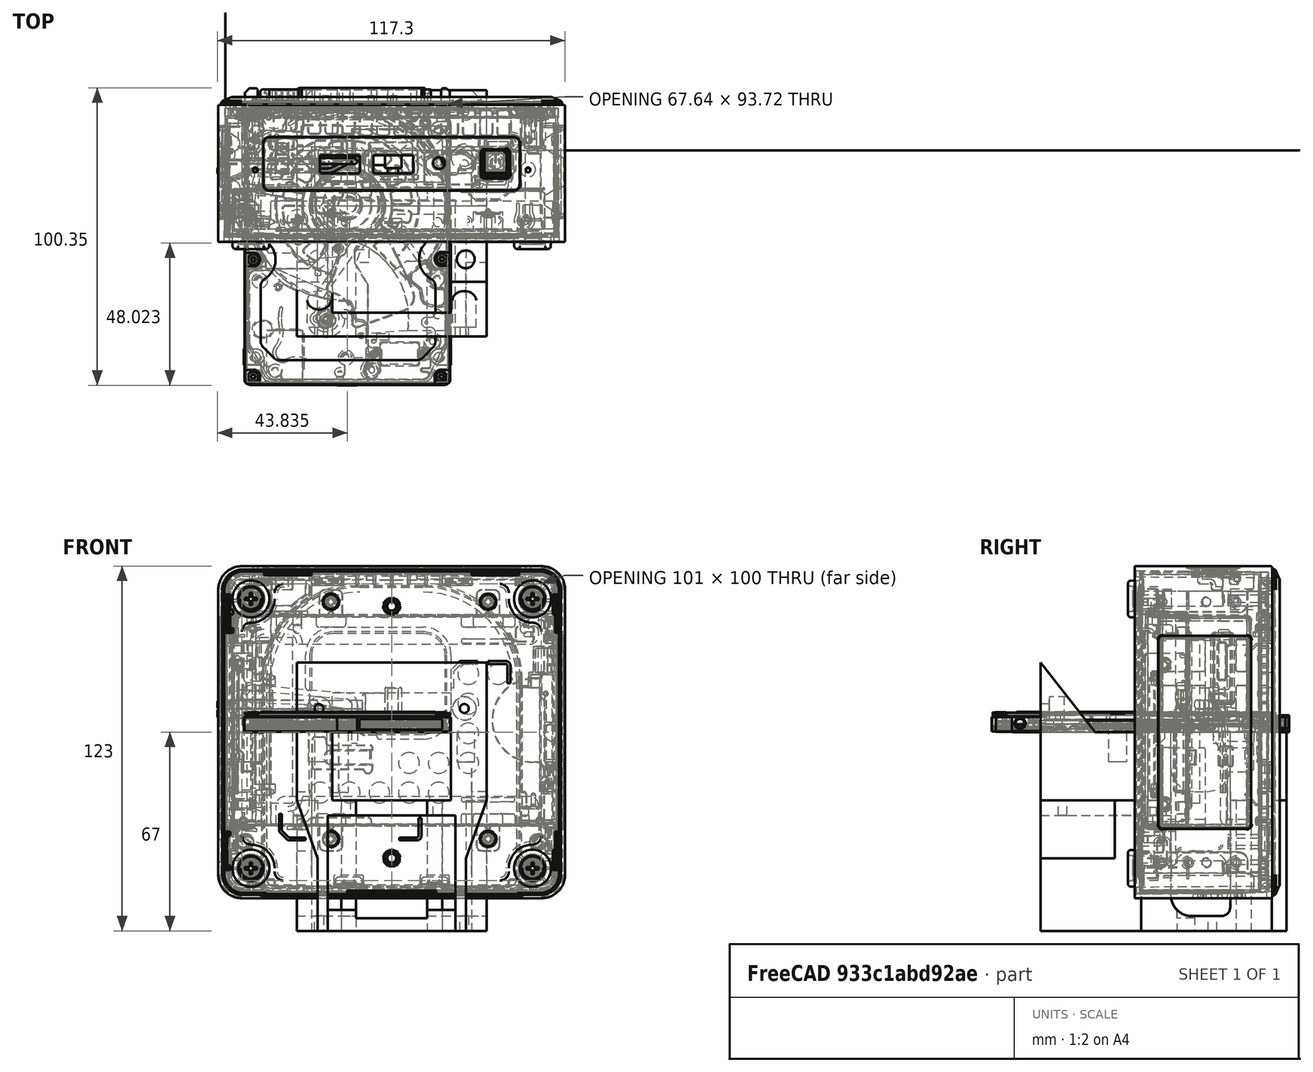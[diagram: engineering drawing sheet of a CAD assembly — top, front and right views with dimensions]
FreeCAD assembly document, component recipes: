
FREECAD ASSEMBLY — COMPONENT RECIPES ("RobotBody")

This assembly document has 14 components, labeled P0..P13 below (a component is one placed body or linked part). 12 of them carry a construction recipe — the FreeCAD feature program that regenerates the part from scratch, quoted from this document or its linked companion documents; the rest are supplied as boundary geometry only. No exploded tour is included for this assembly.
COMPONENT P0 — recipe-attached ("BodyHolder001", modeled in this document).
Construction recipe (the document's own serialized feature program — sketch geometry with constraints, then the solid features built on it; lengths are millimeters unless a unit is written):

FEATURE [Sketcher::SketchObject] Sketch022
  ArcFitTolerance = 1e-06
  AttachmentSupport = -> [XY_Plane002]
  FullyConstrained = false
  MakeInternals = false
  MapMode = 5
  expr: Constraints[10] = <<SpreadSheet001>>.BaseWidth
  expr: Constraints[18] = <<SpreadSheet001>>.BaseRectWidth
  expr: Constraints[23] = <<SpreadSheet001>>.BaseWidth / 2
  sketch-geometry (10):
    g0: GeomPoint [constr] X=0 Y=0 Z=0
    g1: LineSegment StartX=32 StartY=-51 StartZ=0 EndX=32 EndY=32 EndZ=0
    g2: LineSegment StartX=32 StartY=32 StartZ=0 EndX=-32 EndY=32 EndZ=0
    g3: LineSegment StartX=-32 StartY=32 StartZ=0 EndX=-32 EndY=-51 EndZ=0
    g4: LineSegment StartX=-32 StartY=-51 StartZ=0 EndX=-20 EndY=-51 EndZ=0
    g5: GeomPoint [constr] X=0 Y=0 Z=0
    g6: LineSegment StartX=20 StartY=-51 StartZ=0 EndX=32 EndY=-51 EndZ=0
    g7: LineSegment StartX=-20 StartY=20 StartZ=0 EndX=-20 EndY=-51 EndZ=0
    g8: LineSegment StartX=20 StartY=20 StartZ=0 EndX=20 EndY=-51 EndZ=0
    g9: LineSegment StartX=-20 StartY=20 StartZ=0 EndX=20 EndY=20 EndZ=0
  constraints (25):
    c: Coincident(g0,g-1)
    c: Coincident(g1,g2)
    c: Coincident(g2,g3)
    c: Coincident(g3,g4)
    c: Coincident(g6,g1)
    c: Vertical(g1)
    c: Vertical(g3)
    c: Horizontal(g2)
    c: Horizontal(g4)
    c: Coincident(g5,g0)
    c: DistanceX(g2,g2) = 64
    c: Horizontal(g6,g1)
    c: Coincident(g7,g4)
    c: Vertical(g7)
    c: Coincident(g8,g6)
    c: Vertical(g8)
    c: Horizontal(g8,g7)
    c: Horizontal(g4,g6)
    c: Distance(g8,g7) = 40
    c: Equal(g4,g6)
    c: Coincident(g7,g9)
    c: Coincident(g9,g8)
    c: Distance(g2,g9) = 12
    c: Distance(g-1,g2) = 32
    c: Distance(g-1,g4) = 51
FEATURE [PartDesign::Pad] Pad009
  Direction = (0,0,1)
  Length = 23
  Length2 = 10
  Profile = -> Sketch022
  ReferenceAxis = -> Sketch022 [N_Axis]
  Refine = true
  Reversed = true
  Suppressed = false
  Type = 0
  expr: Length = <<SpreadSheet001>>.MainShaftHolder
FEATURE [Sketcher::SketchObject] Sketch023
  ArcFitTolerance = 1e-06
  AttachmentSupport = -> [Pad009]
  FullyConstrained = false
  MakeInternals = false
  MapMode = 5
  Placement = pos=(0,0,-23) rot=(1,0,0;3.14159rad)
  sketch-geometry (9):
    g0: LineSegment StartX=-25 StartY=51 StartZ=0 EndX=-25 EndY=-1 EndZ=0
    g1: LineSegment StartX=-25 StartY=-1 StartZ=0 EndX=25 EndY=-1 EndZ=0
    g2: LineSegment StartX=25 StartY=-1 StartZ=0 EndX=25 EndY=51 EndZ=0
    g3: LineSegment StartX=25 StartY=51 StartZ=0 EndX=12 EndY=51 EndZ=0
    g4: GeomPoint [constr] X=0 Y=28 Z=0
    g5: ArcOfCircle CenterX=0 CenterY=28 CenterZ=0 NormalX=0 NormalY=0 NormalZ=1 AngleXU=0 Radius=12 StartAngle=3.14094 EndAngle=6.28253
    g6: LineSegment StartX=-12 StartY=28.0078 StartZ=0 EndX=-12 EndY=51 EndZ=0
    g7: LineSegment StartX=12 StartY=27.9922 StartZ=0 EndX=12 EndY=51 EndZ=0
    g8: LineSegment StartX=-12 StartY=51 StartZ=0 EndX=-25 EndY=51 EndZ=0
  constraints (24):
    c: Coincident(g0,g1)
    c: Coincident(g1,g2)
    c: Coincident(g2,g3)
    c: Coincident(g8,g0)
    c: Vertical(g0)
    c: Vertical(g2)
    c: Horizontal(g1)
    c: PointOnObject(g4,g-2)
    c: DistanceY(g-1,g4) = 28
    c: DistanceX(g8,g3) = 50
    c: Angle(g5) = 3.14159
    c: Coincident(g5,g4)
    c: Vertical(g6)
    c: Coincident(g6,g5)
    c: Radius(g5) = 12
    c: Coincident(g5,g7)
    c: Coincident(g7,g3)
    c: Vertical(g7)
    c: Equal(g0,g2)
    c: Horizontal(g3)
    c: Horizontal(g8)
    c: Coincident(g6,g8)
    c: Distance(g4,g3) = 23
    c: Distance(g4,g1) = 29
FEATURE [PartDesign::Pad] Pad010
  BaseFeature = -> Pad009
  Direction = (0,0,-1)
  Length = 44
  Length2 = 10
  Profile = -> Sketch023
  ReferenceAxis = -> Sketch023 [N_Axis]
  Refine = true
  Suppressed = false
  Type = 0
FEATURE [Sketcher::SketchObject] Sketch024
  ArcFitTolerance = 1e-06
  AttachmentSupport = -> [Pad010]
  FullyConstrained = false
  MakeInternals = false
  MapMode = 5
  Placement = pos=(0,-51,0) rot=(1,0,0;1.5708rad)
  sketch-geometry (5):
    g0: LineSegment StartX=21.4848 StartY=-78 StartZ=0 EndX=21.4848 EndY=-28 EndZ=0
    g1: LineSegment StartX=21.4848 StartY=-28 StartZ=0 EndX=-21.5152 EndY=-28 EndZ=0
    g2: LineSegment StartX=-21.5152 StartY=-28 StartZ=0 EndX=-21.5152 EndY=-78 EndZ=0
    g3: LineSegment StartX=-21.5152 StartY=-78 StartZ=0 EndX=21.4848 EndY=-78 EndZ=0
    g4: GeomPoint [constr] X=-0.0151564 Y=-53 Z=0
  constraints (12):
    c: Coincident(g0,g1)
    c: Coincident(g1,g2)
    c: Coincident(g2,g3)
    c: Coincident(g3,g0)
    c: Vertical(g0)
    c: Vertical(g2)
    c: Horizontal(g1)
    c: Horizontal(g3)
    c: Symmetric(g2,g0,g4)
    c: DistanceY(g2,g2) = 50
    c: DistanceX(g1,g1) = 43
    c: Distance(g-1,g1) = 28
FEATURE [PartDesign::Pocket] Pocket012
  BaseFeature = -> Pad010
  Direction = (0,1,-2e-16)
  Length = 46
  Length2 = 5
  Profile = -> Sketch024
  ReferenceAxis = -> Sketch024 [N_Axis]
  Refine = true
  Suppressed = false
  Type = 0
FEATURE [Sketcher::SketchObject] Sketch025
  ArcFitTolerance = 1e-06
  AttachmentSupport = -> [Pocket012]
  ExternalGeometry = -> [Pocket012]
  FullyConstrained = false
  MakeInternals = false
  MapMode = 5
  Placement = pos=(0,-51,0) rot=(1,0,0;1.5708rad)
  sketch-geometry (6):
    g0: LineSegment StartX=-32 StartY=-23 StartZ=0 EndX=-25 EndY=-23 EndZ=0
    g1: LineSegment StartX=-25 StartY=-23 StartZ=0 EndX=-25 EndY=-42.5619 EndZ=0
    g2: LineSegment StartX=-25 StartY=-42.5619 StartZ=0 EndX=-32 EndY=-23 EndZ=0
    g3: LineSegment StartX=32 StartY=-23 StartZ=0 EndX=25 EndY=-23 EndZ=0
    g4: LineSegment StartX=25 StartY=-42.5619 StartZ=0 EndX=32 EndY=-23 EndZ=0
    g5: LineSegment StartX=25 StartY=-23 StartZ=0 EndX=25 EndY=-42.5619 EndZ=0
  constraints (13):
    c: Coincident(g-3,g0)
    c: Coincident(g0,g-4)
    c: Coincident(g0,g1)
    c: Vertical(g1)
    c: Coincident(g1,g2)
    c: Coincident(g2,g0)
    c: Coincident(g-6,g3)
    c: Coincident(g3,g-6)
    c: Coincident(g4,g3)
    c: Coincident(g3,g5)
    c: Coincident(g5,g4)
    c: Vertical(g5)
    c: Horizontal(g1,g4)
FEATURE [PartDesign::Pad] Pad011
  BaseFeature = -> Pocket012
  Direction = (0,-1,2e-16)
  Length = 25
  Length2 = 10
  Profile = -> Sketch025
  ReferenceAxis = -> Sketch025 [N_Axis]
  Refine = true
  Reversed = true
  Suppressed = false
  Type = 0
FEATURE [Sketcher::SketchObject] Sketch026
  ArcFitTolerance = 1e-06
  AttachmentSupport = -> [Pad011]
  FullyConstrained = true
  MakeInternals = false
  MapMode = 5
  Placement = pos=(0,0,-23) rot=(0,0,1;0rad)
  expr: Constraints[10] = <<SpreadSheet001>>.StepperCenterToScewHole
  expr: Constraints[11] = <<SpreadSheet001>>.StepperCenterToScewHole
  expr: Constraints[12] = <<SpreadSheet001>>.StepperCenterToScewHole
  expr: Constraints[13] = <<SpreadSheet001>>.StepperCenterToScewHole
  expr: Constraints[3] = <<SpreadSheet001>>.StepperCenterToScewHole
  expr: Constraints[4] = <<SpreadSheet001>>.StepperCenterToScewHole
  expr: Constraints[8] = <<SpreadSheet001>>.StepperCenterToScewHole
  expr: Constraints[9] = <<SpreadSheet001>>.StepperCenterToScewHole
  sketch-geometry (5):
    g0: GeomPoint [constr] X=0 Y=-28 Z=0
    g1: Circle CenterX=-15.5 CenterY=-12.5 CenterZ=0 NormalX=0 NormalY=0 NormalZ=1 AngleXU=0 Radius=1.5
    g2: Circle CenterX=-15.5 CenterY=-43.5 CenterZ=0 NormalX=0 NormalY=0 NormalZ=1 AngleXU=0 Radius=1.5
    g3: Circle CenterX=15.5 CenterY=-43.5 CenterZ=0 NormalX=0 NormalY=0 NormalZ=1 AngleXU=0 Radius=1.5
    g4: Circle CenterX=15.5 CenterY=-12.5 CenterZ=0 NormalX=0 NormalY=0 NormalZ=1 AngleXU=0 Radius=1.5
  constraints (14):
    c: PointOnObject(g0,g-2)
    c: DistanceY(g0,g-1) = 28
    c: Diameter(g1) = 3
    c: Distance(g1,g-2) = 15.5
    c: DistanceY(g0,g1) = 15.5
    c: Diameter(g2) = 3
    c: Diameter(g3) = 3
    c: Diameter(g4) = 3
    c: Distance(g4,g-2) = 15.5
    c: DistanceY(g0,g4) = 15.5
    c: DistanceY(g3,g0) = 15.5
    c: DistanceY(g2,g0) = 15.5
    c: DistanceX(g2,g0) = 15.5
    c: DistanceX(g0,g3) = 15.5
FEATURE [PartDesign::Pocket] Pocket013
  BaseFeature = -> Pad011
  Direction = (0,0,-1)
  Length = 10
  Length2 = 5
  Profile = -> Sketch026
  ReferenceAxis = -> Sketch026 [N_Axis]
  Refine = true
  Suppressed = false
  Type = 1
FEATURE [Sketcher::SketchObject] Sketch027
  ArcFitTolerance = 1e-06
  AttachmentSupport = -> [Pocket013]
  FullyConstrained = true
  MakeInternals = false
  MapMode = 5
  expr: Constraints[0] = 6
  expr: Constraints[1] = 25
  expr: Constraints[2] = 25 mm
  sketch-geometry (1):
    g0: Circle CenterX=-25 CenterY=25 CenterZ=0 NormalX=0 NormalY=0 NormalZ=1 AngleXU=0 Radius=3
  constraints (3):
    c: Diameter(g0) = 6
    c: Distance(g0,g-2) = 25
    c: Distance(g0,g-1) = 25
FEATURE [PartDesign::Pocket] Pocket014
  BaseFeature = -> Pocket013
  Direction = (0,0,-1)
  Length = 10
  Length2 = 5
  Profile = -> Sketch027
  ReferenceAxis = -> Sketch027 [N_Axis]
  Refine = true
  Suppressed = false
  Type = 0
FEATURE [PartDesign::PolarPattern] PolarPattern001
  Angle = 360
  Axis = -> Sketch027 [N_Axis]
  BaseFeature = -> Pocket014
  Mode = 0
  Occurrences = 4
  Offset = 120
  Originals = -> [Pocket014]
  Refine = true
  Suppressed = false
  TransformMode = 0
FEATURE [Sketcher::SketchObject] Sketch028
  ArcFitTolerance = 1e-06
  AttachmentSupport = -> [PolarPattern001]
  FullyConstrained = false
  MakeInternals = false
  MapMode = 5
  Placement = pos=(0,1,0) rot=(0,0.707107,0.707107;3.14159rad)
  sketch-geometry (4):
    g0: LineSegment StartX=-12 StartY=-62.7172 StartZ=0 EndX=12 EndY=-62.7172 EndZ=0
    g1: LineSegment StartX=12 StartY=-62.7172 StartZ=0 EndX=12 EndY=-49.3568 EndZ=0
    g2: LineSegment StartX=-12 StartY=-49.3568 StartZ=0 EndX=-12 EndY=-62.7172 EndZ=0
    g3: ArcOfCircle CenterX=5.51344e-07 CenterY=-49.3568 CenterZ=0 NormalX=0 NormalY=0 NormalZ=1 AngleXU=0 Radius=12 StartAngle=4e-16 EndAngle=3.14159
  constraints (10):
    c: Coincident(g0,g1)
    c: Coincident(g2,g0)
    c: Horizontal(g0)
    c: Vertical(g1)
    c: Vertical(g2)
    c: Distance(g1,g2) = 24
    c: Coincident(g0,g-3)
    c: Symmetric(g1,g2,g3)
    c: Coincident(g3,g2)
    c: Coincident(g3,g1)
FEATURE [PartDesign::Pocket] Pocket011
  BaseFeature = -> PolarPattern001
  Direction = (0,-1,2e-16)
  Length = 6
  Length2 = 5
  Profile = -> Sketch028
  ReferenceAxis = -> Sketch028 [N_Axis]
  Refine = true
  Suppressed = false
  Type = 0
FEATURE [Sketcher::SketchObject] Sketch021
  ArcFitTolerance = 1e-06
  AttachmentSupport = -> [Pocket011]
  FullyConstrained = true
  MakeInternals = false
  MapMode = 5
  Placement = pos=(0,0,-23) rot=(1,0,0;3.14159rad)
  sketch-geometry (16):
    g0: LineSegment StartX=-32 StartY=17 StartZ=0 EndX=-25 EndY=17 EndZ=0
    g1: LineSegment StartX=-25 StartY=17 StartZ=0 EndX=-25 EndY=7 EndZ=0
    g2: LineSegment StartX=-25 StartY=7 StartZ=0 EndX=-17 EndY=-1 EndZ=0
    g3: LineSegment StartX=-17 StartY=-1 StartZ=0 EndX=-17 EndY=-15 EndZ=0
    g4: LineSegment StartX=-17 StartY=-15 StartZ=0 EndX=-12 EndY=-20 EndZ=0
    g5: LineSegment StartX=-12 StartY=-20 StartZ=0 EndX=12 EndY=-20 EndZ=0
    g6: LineSegment StartX=12 StartY=-20 StartZ=0 EndX=17 EndY=-15 EndZ=0
    g7: LineSegment StartX=17 StartY=-15 StartZ=0 EndX=17 EndY=-1 EndZ=0
    g8: LineSegment StartX=17 StartY=-1 StartZ=0 EndX=25 EndY=7 EndZ=0
    g9: LineSegment StartX=25 StartY=7 StartZ=0 EndX=25 EndY=17 EndZ=0
    g10: LineSegment StartX=25 StartY=17 StartZ=0 EndX=32 EndY=17 EndZ=0
    g11: LineSegment StartX=32 StartY=17 StartZ=0 EndX=32 EndY=-27 EndZ=0
    g12: LineSegment StartX=32 StartY=-27 StartZ=0 EndX=27 EndY=-32 EndZ=0
    g13: LineSegment StartX=27 StartY=-32 StartZ=0 EndX=-27 EndY=-32 EndZ=0
    g14: LineSegment StartX=-27 StartY=-32 StartZ=0 EndX=-32 EndY=-27 EndZ=0
    g15: LineSegment StartX=-32 StartY=-27 StartZ=0 EndX=-32 EndY=17 EndZ=0
  constraints (48):
    c: Horizontal(g0)
    c: Coincident(g0,g1)
    c: Vertical(g1)
    c: Coincident(g1,g2)
    c: Coincident(g2,g3)
    c: Vertical(g3)
    c: Coincident(g3,g4)
    c: Coincident(g4,g5)
    c: Horizontal(g5)
    c: Coincident(g5,g6)
    c: Coincident(g6,g7)
    c: Vertical(g7)
    c: Coincident(g7,g8)
    c: Coincident(g8,g9)
    c: Vertical(g9)
    c: Coincident(g9,g10)
    c: Horizontal(g10)
    c: Coincident(g10,g11)
    c: Vertical(g11)
    c: Coincident(g11,g12)
    c: Coincident(g12,g13)
    c: Horizontal(g13)
    c: Coincident(g13,g14)
    c: Coincident(g14,g15)
    c: Coincident(g15,g0)
    c: Vertical(g15)
    c: Distance(g-2,g15) = 32
    c: Distance(g-1,g0) = 17
    c: Distance(g0,g0) = 7
    c: DistanceY(g1,g1) = 10
    c: Distance(g15,g3) = 15
    c: Angle(g2,g1) = 2.35619
    c: Angle(g14,g15) = 2.35619
    c: Distance(g-1,g13) = 32
    c: DistanceX(g10,g10) = 7
    c: Distance(g-2,g11) = 32
    c: DistanceY(g9,g9) = 10
    c: Angle(g9,g8) = 2.35619
    c: Distance(g-1,g10) = 17
    c: Distance(g7,g11) = 15
    c: DistanceY(g14,g-1) = 27
    c: DistanceY(g11,g-1) = 27
    c: Angle(g11,g12) = 2.35619
    c: Angle(g4,g3) = 2.35619
    c: Angle(g7,g6) = 2.35619
    c: Distance(g-1,g5) = 20
    c: DistanceX(g4,g-1) = 12
    c: Distance(g5,g-2) = 12
FEATURE [PartDesign::Pad] Pad008
  BaseFeature = -> Pocket011
  Direction = (0,0,-1)
  Length = 44
  Length2 = 10
  Profile = -> Sketch021
  ReferenceAxis = -> Sketch021 [N_Axis]
  Refine = true
  Suppressed = false
  Type = 0
FEATURE [Sketcher::SketchObject] Sketch029
  ArcFitTolerance = 1e-06
  AttachmentSupport = -> [Pad008]
  ExternalGeometry = -> [Pad008]
  FullyConstrained = true
  MakeInternals = false
  MapMode = 5
  Placement = pos=(-32,3.571e-13,-2.7539e-12) rot=(-0.57735,0.57735,0.57735;4.18879rad)
  sketch-geometry (5):
    g0: LineSegment StartX=7 StartY=0 StartZ=0 EndX=-13 EndY=0 EndZ=0
    g1: LineSegment StartX=7 StartY=-55 StartZ=0 EndX=7 EndY=0 EndZ=0
    g2: LineSegment StartX=-13 StartY=-62 StartZ=0 EndX=-13 EndY=0 EndZ=0
    g3: LineSegment StartX=-13 StartY=-62 StartZ=0 EndX=-1.8e-15 EndY=-62 EndZ=0
    g4: ArcOfCircle CenterX=0 CenterY=-55 CenterZ=0 NormalX=0 NormalY=0 NormalZ=1 AngleXU=0 Radius=7 StartAngle=4.71239 EndAngle=6.28319
  constraints (16):
    c: Horizontal(g0)
    c: Coincident(g1,g0)
    c: Vertical(g1)
    c: Distance(g0,g-2) = 13
    c: DistanceY(g1,g1) = 55
    c: Coincident(g2,g0)
    c: Vertical(g2)
    c: Coincident(g2,g3)
    c: DistanceX(g3,g3) = 13
    c: Horizontal(g3)
    c: Distance(g-3,g3) = 5
    c: Horizontal(g0,g-1)
    c: PointOnObject(g4,g-2)
    c: Coincident(g4,g1)
    c: Coincident(g3,g4)
    c: Horizontal(g4,g1)
FEATURE [PartDesign::Pocket] Pocket015
  BaseFeature = -> Pad008
  Direction = (1,-1.11e-14,8.62e-14)
  Length = 25
  Length2 = 5
  Profile = -> Sketch029
  ReferenceAxis = -> Sketch029 [N_Axis]
  Refine = true
  Suppressed = false
  Type = 1
FEATURE [Sketcher::SketchObject] Sketch031
  ArcFitTolerance = 1e-06
  AttachmentSupport = -> [Pocket015]
  ExternalGeometry = -> [Pocket015]
  FullyConstrained = false
  MakeInternals = false
  MapMode = 5
  Placement = pos=(-32,3.571e-13,-2.7539e-12) rot=(-0.57735,0.57735,0.57735;4.18879rad)
  sketch-geometry (3):
    g0: LineSegment StartX=51 StartY=0 StartZ=0 EndX=51 EndY=23.5446 EndZ=0
    g1: LineSegment StartX=51 StartY=23.5446 StartZ=0 EndX=32.5692 EndY=0 EndZ=0
    g2: LineSegment StartX=32.5692 StartY=0 StartZ=0 EndX=51 EndY=0 EndZ=0
  constraints (6):
    c: Coincident(g-4,g0)
    c: Vertical(g0)
    c: Coincident(g0,g1)
    c: PointOnObject(g1,g-4)
    c: Coincident(g1,g2)
    c: Coincident(g2,g0)
FEATURE [PartDesign::Pad] Pad013
  BaseFeature = -> Pocket015
  Direction = (-1,1.11e-14,-8.62e-14)
  Length = 64
  Length2 = 10
  Profile = -> Sketch031
  ReferenceAxis = -> Sketch031 [N_Axis]
  Refine = true
  Reversed = true
  Suppressed = false
  Type = 0
FEATURE [Sketcher::SketchObject] Sketch032
  ArcFitTolerance = 1e-06
  AttachmentSupport = -> [Pad013]
  ExternalGeometry = -> [Pad013]
  FullyConstrained = true
  MakeInternals = false
  MapMode = 5
  Placement = pos=(0,0,2.8e-15) rot=(1,0,0;3.14159rad)
  sketch-geometry (4):
    g0: LineSegment StartX=20 StartY=32.5692 StartZ=0 EndX=20 EndY=43 EndZ=0
    g1: LineSegment StartX=20 StartY=43 StartZ=0 EndX=-20 EndY=43 EndZ=0
    g2: LineSegment StartX=-20 StartY=43 StartZ=0 EndX=-20 EndY=32.5692 EndZ=0
    g3: LineSegment StartX=-20 StartY=32.5692 StartZ=0 EndX=20 EndY=32.5692 EndZ=0
  constraints (11):
    c: Coincident(g0,g1)
    c: Coincident(g1,g2)
    c: Coincident(g2,g3)
    c: Coincident(g3,g0)
    c: Vertical(g0)
    c: Vertical(g2)
    c: Horizontal(g1)
    c: Horizontal(g3)
    c: Coincident(g0,g-4)
    c: PointOnObject(g1,g-5)
    c: Distance(g-3,g1) = 8
FEATURE [PartDesign::Pocket] Pocket016
  BaseFeature = -> Pad013
  Direction = (-8.62e-14,0,1)
  Length = 10
  Length2 = 5
  Profile = -> Sketch032
  ReferenceAxis = -> Sketch032 [N_Axis]
  Refine = true
  Suppressed = false
  Type = 1
FEATURE [Sketcher::SketchObject] Sketch033
  ArcFitTolerance = 1e-06
  AttachmentSupport = -> [Pocket016]
  FullyConstrained = true
  MakeInternals = false
  MapMode = 5
  Placement = pos=(-2.356e-13,-51,0) rot=(1,0,0;1.5708rad)
  sketch-geometry (2):
    g0: Circle CenterX=-24.5 CenterY=8 CenterZ=0 NormalX=0 NormalY=0 NormalZ=1 AngleXU=0 Radius=1.5
    g1: Circle CenterX=24.5 CenterY=8 CenterZ=0 NormalX=0 NormalY=0 NormalZ=1 AngleXU=0 Radius=1.5
  constraints (6):
    c: Diameter(g0) = 3
    c: Diameter(g1) = 3
    c: DistanceY(g-1,g1) = 8
    c: DistanceY(g-1,g0) = 8
    c: DistanceX(g0,g-1) = 24.5
    c: DistanceX(g-1,g1) = 24.5
FEATURE [PartDesign::Pocket] Pocket017
  BaseFeature = -> Pocket016
  Direction = (4.6e-15,1,-2e-16)
  Length = 5
  Length2 = 5
  Profile = -> Sketch033
  ReferenceAxis = -> Sketch033 [N_Axis]
  Refine = true
  Suppressed = false
  Type = 1
FEATURE [Sketcher::SketchObject] Sketch034
  ArcFitTolerance = 1e-06
  AttachmentOffset = pos=(0,0,-3) rot=(0,0,1;0rad)
  AttachmentSupport = -> [Pocket017]
  FullyConstrained = true
  MakeInternals = false
  MapMode = 5
  Placement = pos=(-2.218e-13,-48,-7e-16) rot=(1,0,0;1.5708rad)
  sketch-geometry (2):
    g0: Circle CenterX=-24.5 CenterY=8 CenterZ=0 NormalX=0 NormalY=0 NormalZ=1 AngleXU=0 Radius=4
    g1: Circle CenterX=24.5 CenterY=8 CenterZ=0 NormalX=0 NormalY=0 NormalZ=1 AngleXU=0 Radius=4
  constraints (6):
    c: Diameter(g0) = 8
    c: DistanceY(g-1,g0) = 8
    c: DistanceX(g0,g-1) = 24.5
    c: Diameter(g1) = 8
    c: DistanceY(g-1,g1) = 8
    c: DistanceX(g-1,g1) = 24.5
FEATURE [PartDesign::Pocket] Pocket018
  BaseFeature = -> Pocket017
  Direction = (4.6e-15,1,-2e-16)
  Length = 5
  Length2 = 5
  Profile = -> Sketch034
  ReferenceAxis = -> Sketch034 [N_Axis]
  Refine = true
  Suppressed = false
  Type = 1
FEATURE [Sketcher::SketchObject] Sketch036
  ArcFitTolerance = 1e-06
  AttachmentSupport = -> [Pocket018]
  FullyConstrained = true
  MakeInternals = false
  MapMode = 5
  Placement = pos=(5.3413e-12,0,-62) rot=(0,0,1;0rad)
  sketch-geometry (2):
    g0: Circle CenterX=24.5 CenterY=7 CenterZ=0 NormalX=0 NormalY=0 NormalZ=1 AngleXU=0 Radius=1.5
    g1: Circle CenterX=-24.5 CenterY=7 CenterZ=0 NormalX=0 NormalY=0 NormalZ=1 AngleXU=0 Radius=1.5
  constraints (6):
    c: Diameter(g0) = 3
    c: Diameter(g1) = 3
    c: DistanceX(g1,g-1) = 24.5
    c: DistanceY(g-1,g1) = 7
    c: DistanceX(g-1,g0) = 24.5
    c: DistanceY(g-1,g0) = 7
FEATURE [PartDesign::Pocket] Pocket019
  BaseFeature = -> Pocket018
  Direction = (8.62e-14,0,-1)
  Length = 5
  Length2 = 5
  Profile = -> Sketch036
  ReferenceAxis = -> Sketch036 [N_Axis]
  Refine = true
  Suppressed = false
  Type = 0
FEATURE [Sketcher::SketchObject] Sketch037
  ArcFitTolerance = 1e-06
  AttachmentSupport = -> [Pocket019]
  FullyConstrained = true
  MakeInternals = false
  MapMode = 5
  sketch-geometry (2):
    g0: Circle CenterX=-24.5 CenterY=7 CenterZ=0 NormalX=0 NormalY=0 NormalZ=1 AngleXU=0 Radius=3
    g1: Circle CenterX=24.5 CenterY=7 CenterZ=0 NormalX=0 NormalY=0 NormalZ=1 AngleXU=0 Radius=3
  constraints (6):
    c: Diameter(g0) = 6
    c: Diameter(g1) = 6
    c: DistanceY(g-1,g0) = 7
    c: DistanceX(g0,g-1) = 24.5
    c: DistanceY(g-1,g1) = 7
    c: DistanceX(g-1,g1) = 24.5
FEATURE [PartDesign::Pocket] Pocket020
  BaseFeature = -> Pocket019
  Direction = (0,0,-1)
  Length = 10
  Length2 = 5
  Profile = -> Sketch037
  ReferenceAxis = -> Sketch037 [N_Axis]
  Refine = true
  Suppressed = false
  Type = 0
FEATURE [Sketcher::SketchObject] Sketch052
  ArcFitTolerance = 1e-06
  AttachmentSupport = -> [Pocket020]
  ExternalGeometry = -> [Pocket020]
  FullyConstrained = false
  MakeInternals = false
  MapMode = 5
  Placement = pos=(32,-4.915e-13,2.7002e-12) rot=(0.57735,0.57735,0.57735;2.0944rad)
  sketch-geometry (4):
    g0: LineSegment StartX=-7 StartY=-20 StartZ=0 EndX=-7 EndY=-40 EndZ=0
    g1: LineSegment StartX=-7 StartY=-40 StartZ=0 EndX=13 EndY=-40 EndZ=0
    g2: LineSegment StartX=-7 StartY=-20 StartZ=0 EndX=13 EndY=-20 EndZ=0
    g3: LineSegment StartX=13 StartY=-20 StartZ=0 EndX=13 EndY=-40 EndZ=0
  constraints (11):
    c: PointOnObject(g0,g-3)
    c: PointOnObject(g0,g-3)
    c: PointOnObject(g1,g-4)
    c: Coincident(g2,g3)
    c: Coincident(g3,g1)
    c: Horizontal(g1)
    c: Horizontal(g2)
    c: Vertical(g3)
    c: Distance(g-1,g2) = 20
    c: Coincident(g0,g2)
    c: DistanceY(g3,g3) = 20
FEATURE [PartDesign::Pad] Pad024
  BaseFeature = -> Pocket020
  Direction = (1,-1.52e-14,8.43e-14)
  Length = 5
  Length2 = 10
  Profile = -> Sketch052
  ReferenceAxis = -> Sketch052 [N_Axis]
  Refine = true
  Reversed = true
  Suppressed = false
  Type = 0
FEATURE [PartDesign::Mirrored] Mirrored002
  BaseFeature = -> Pad024
  MirrorPlane = -> YZ_Plane002
  Originals = -> [Pad024]
  Refine = true
  Suppressed = false
  TransformMode = 0
FEATURE [PartDesign::Fillet] Fillet
  Base = -> Mirrored002 [Edge182,Edge78,Edge80,Edge184,Edge176,Edge58,Edge174,Edge56]
  BaseFeature = -> Mirrored002
  Radius = 8
  Refine = true
  SupportTransform = false
  Suppressed = false
  UseAllEdges = false
FEATURE [PartDesign::Fillet] Fillet001
  Base = -> Fillet [Edge172,Edge3]
  BaseFeature = -> Fillet
  Radius = 3
  Refine = true
  SupportTransform = false
  Suppressed = false
  UseAllEdges = false
FEATURE [PartDesign::Body] Body002  label="BodyHolder001"
  AllowCompound = false
  Group = -> [Sketch022,Pad009,Sketch023,Pad010,Sketch024,Pocket012,Sketch025,Pad011,Sketch026,Pocket013,Sketch027,Pocket014,PolarPattern001,Sketch028,Pocket011,Sketch021,Pad008,Sketch029,Pocket015,Sketch031,Pad013,Sketch032,Pocket016,Sketch033,Pocket017,Sketch034,Pocket018,Sketch036,Pocket019,Sketch037,Pocket020,Sketch052,Pad024,Mirrored002,Fillet,Fillet001]
  Origin = -> Origin002
  Tip = -> Fillet001
COMPONENT P1 — recipe-attached ("MainShaft", modeled in this document).
Construction recipe (the document's own serialized feature program — sketch geometry with constraints, then the solid features built on it; lengths are millimeters unless a unit is written):

FEATURE [Sketcher::SketchObject] Sketch030
  ArcFitTolerance = 1e-06
  AttachmentSupport = -> [XY_Plane]
  FullyConstrained = false
  MakeInternals = false
  MapMode = 5
  sketch-geometry (21):
    g0: LineSegment StartX=-7.5 StartY=-7.5 StartZ=0 EndX=-3 EndY=-7.5 EndZ=0
    g1: LineSegment StartX=7.5 StartY=-7.5 StartZ=0 EndX=7.5 EndY=-3 EndZ=0
    g2: LineSegment StartX=7.5 StartY=7.5 StartZ=0 EndX=3 EndY=7.5 EndZ=0
    g3: LineSegment StartX=-7.5 StartY=7.5 StartZ=0 EndX=-7.5 EndY=3 EndZ=0
    g4: GeomPoint [constr] X=0 Y=0 Z=0
    g5: LineSegment StartX=3 StartY=-7.5 StartZ=0 EndX=3 EndY=-4 EndZ=0
    g6: LineSegment StartX=3 StartY=-4 StartZ=0 EndX=-3 EndY=-4 EndZ=0
    g7: LineSegment StartX=-3 StartY=-4 StartZ=0 EndX=-3 EndY=-7.5 EndZ=0
    g8: LineSegment StartX=7.5 StartY=-3 StartZ=0 EndX=4 EndY=-3 EndZ=0
    g9: LineSegment StartX=4 StartY=-3 StartZ=0 EndX=4 EndY=3 EndZ=0
    g10: LineSegment StartX=4 StartY=3 StartZ=0 EndX=7.5 EndY=3 EndZ=0
    g11: LineSegment StartX=3 StartY=7.5 StartZ=0 EndX=3 EndY=4 EndZ=0
    g12: LineSegment StartX=3 StartY=4 StartZ=0 EndX=-3 EndY=4 EndZ=0
    g13: LineSegment StartX=-3 StartY=4 StartZ=0 EndX=-3 EndY=7.5 EndZ=0
    g14: LineSegment StartX=-7.5 StartY=3 StartZ=0 EndX=-4 EndY=3 EndZ=0
    g15: LineSegment StartX=-4 StartY=3 StartZ=0 EndX=-4 EndY=-3 EndZ=0
    g16: LineSegment StartX=-4 StartY=-3 StartZ=0 EndX=-7.5 EndY=-3 EndZ=0
    g17: LineSegment StartX=3 StartY=-7.5 StartZ=0 EndX=7.5 EndY=-7.5 EndZ=0
    g18: LineSegment StartX=7.5 StartY=3 StartZ=0 EndX=7.5 EndY=7.5 EndZ=0
    g19: LineSegment StartX=-3 StartY=7.5 StartZ=0 EndX=-7.5 EndY=7.5 EndZ=0
    g20: LineSegment StartX=-7.5 StartY=-3 StartZ=0 EndX=-7.5 EndY=-7.5 EndZ=0
  constraints (56):
    c: Coincident(g17,g1)
    c: Coincident(g18,g2)
    c: Coincident(g19,g3)
    c: Coincident(g20,g0)
    c: Horizontal(g0)
    c: Horizontal(g2)
    c: Vertical(g1)
    c: Vertical(g3)
    c: Symmetric(g2,g0,g4)
    c: Distance(g1,g20) = 15
    c: Distance(g0,g19) = 15
    c: Coincident(g4,g-1)
    c: PointOnObject(g5,g17)
    c: Vertical(g5)
    c: Coincident(g5,g6)
    c: Horizontal(g6)
    c: Coincident(g6,g7)
    c: Vertical(g7)
    c: Horizontal(g8)
    c: Coincident(g8,g9)
    c: Vertical(g9)
    c: Coincident(g9,g10)
    c: PointOnObject(g10,g18)
    c: Horizontal(g10)
    c: Vertical(g11)
    c: Coincident(g11,g12)
    c: Horizontal(g12)
    c: Coincident(g12,g13)
    c: PointOnObject(g13,g19)
    c: Vertical(g13)
    c: Horizontal(g14)
    c: Coincident(g14,g15)
    c: Vertical(g15)
    c: Coincident(g15,g16)
    c: PointOnObject(g16,g20)
    c: Horizontal(g16)
    c: Coincident(g0,g7)
    c: PointOnObject(g17,g5)
    c: Coincident(g1,g8)
    c: PointOnObject(g18,g10)
    c: Coincident(g2,g11)
    c: PointOnObject(g19,g13)
    c: Coincident(g3,g14)
    c: PointOnObject(g20,g16)
    c: Distance(g-1,g6) = 4
    c: Distance(g-2,g15) = 4
    c: Distance(g-1,g12) = 4
    c: Distance(g-2,g9) = 4
    c: Distance(g-2,g5) = 3
    c: Distance(g-1,g8) = 3
    c: Distance(g-1,g10) = 3
    c: Distance(g-2,g7) = 3
    c: Distance(g-1,g16) = 3
    c: Distance(g-1,g14) = 3
    c: Distance(g-2,g13) = 3
    c: Distance(g-2,g11) = 3
FEATURE [PartDesign::Pad] Pad012
  Direction = (0,0,1)
  Length = 150
  Length2 = 10
  Profile = -> Sketch030
  ReferenceAxis = -> Sketch030 [N_Axis]
  Refine = true
  Suppressed = false
  Type = 0
FEATURE [PartDesign::Body] Body  label="Stick150"
  AllowCompound = false
  Group = -> [Sketch030,Pad012]
  Origin = -> Origin
  Placement = pos=(17.1,-58.3,-74.5) rot=(-0.57735,-0.57735,0.57735;2.0944rad)
  Tip = -> Pad012
COMPONENT P2 — recipe-attached ("MainStepper", modeled in this document).
Construction recipe (the document's own serialized feature program — sketch geometry with constraints, then the solid features built on it; lengths are millimeters unless a unit is written):

FEATURE [Sketcher::SketchObject] Sketch005
  ArcFitTolerance = 1e-06
  AttachmentSupport = -> [XY_Plane001]
  FullyConstrained = false
  MakeInternals = false
  MapMode = 5
  expr: Constraints[10] = <<SpreadSheet>>.BaseWidth
  expr: Constraints[18] = <<SpreadSheet>>.BaseRectWidth
  expr: Constraints[23] = <<SpreadSheet>>.BaseWidth / 2
  expr: Constraints[24] = <<SpreadSheet>>.BaseWidth / 2 + 10
  sketch-geometry (10):
    g0: GeomPoint [constr] X=0 Y=0 Z=0
    g1: LineSegment StartX=32 StartY=-42 StartZ=0 EndX=32 EndY=32 EndZ=0
    g2: LineSegment StartX=32 StartY=32 StartZ=0 EndX=-32 EndY=32 EndZ=0
    g3: LineSegment StartX=-32 StartY=32 StartZ=0 EndX=-32 EndY=-42 EndZ=0
    g4: LineSegment StartX=-32 StartY=-42 StartZ=0 EndX=-20 EndY=-42 EndZ=0
    g5: GeomPoint [constr] X=0 Y=0 Z=0
    g6: LineSegment StartX=20 StartY=-42 StartZ=0 EndX=32 EndY=-42 EndZ=0
    g7: LineSegment StartX=-20 StartY=20 StartZ=0 EndX=-20 EndY=-42 EndZ=0
    g8: LineSegment StartX=20 StartY=20 StartZ=0 EndX=20 EndY=-42 EndZ=0
    g9: LineSegment StartX=-20 StartY=20 StartZ=0 EndX=20 EndY=20 EndZ=0
  constraints (25):
    c: Coincident(g0,g-1)
    c: Coincident(g1,g2)
    c: Coincident(g2,g3)
    c: Coincident(g3,g4)
    c: Coincident(g6,g1)
    c: Vertical(g1)
    c: Vertical(g3)
    c: Horizontal(g2)
    c: Horizontal(g4)
    c: Coincident(g5,g0)
    c: DistanceX(g2,g2) = 64
    c: Horizontal(g6,g1)
    c: Coincident(g7,g4)
    c: Vertical(g7)
    c: Coincident(g8,g6)
    c: Vertical(g8)
    c: Horizontal(g8,g7)
    c: Horizontal(g4,g6)
    c: Distance(g8,g7) = 40
    c: Equal(g4,g6)
    c: Coincident(g7,g9)
    c: Coincident(g9,g8)
    c: Distance(g2,g9) = 12
    c: Distance(g-1,g2) = 32
    c: Distance(g-1,g4) = 42
FEATURE [PartDesign::Pad] Pad004
  Direction = (0,0,1)
  Length = 23
  Length2 = 10
  Profile = -> Sketch005
  ReferenceAxis = -> Sketch005 [N_Axis]
  Refine = true
  Reversed = true
  Suppressed = false
  Type = 0
  expr: Length = <<SpreadSheet>>.MainShaftHolder
FEATURE [Sketcher::SketchObject] Sketch006
  ArcFitTolerance = 1e-06
  AttachmentSupport = -> [Pad004]
  FullyConstrained = false
  MakeInternals = false
  MapMode = 5
  Placement = pos=(0,0,-23) rot=(1,0,0;3.14159rad)
  sketch-geometry (9):
    g0: LineSegment StartX=-25 StartY=57 StartZ=0 EndX=-25 EndY=-1 EndZ=0
    g1: LineSegment StartX=-25 StartY=-1 StartZ=0 EndX=25 EndY=-1 EndZ=0
    g2: LineSegment StartX=25 StartY=-1 StartZ=0 EndX=25 EndY=57 EndZ=0
    g3: LineSegment StartX=25 StartY=57 StartZ=0 EndX=12 EndY=57 EndZ=0
    g4: GeomPoint [constr] X=0 Y=28 Z=0
    g5: ArcOfCircle CenterX=0 CenterY=28 CenterZ=0 NormalX=0 NormalY=0 NormalZ=1 AngleXU=0 Radius=12 StartAngle=3.14162 EndAngle=6.28321
    g6: LineSegment StartX=-12 StartY=27.9997 StartZ=0 EndX=-12 EndY=57 EndZ=0
    g7: LineSegment StartX=12 StartY=28.0003 StartZ=0 EndX=12 EndY=57 EndZ=0
    g8: LineSegment StartX=-12 StartY=57 StartZ=0 EndX=-25 EndY=57 EndZ=0
  constraints (24):
    c: Coincident(g0,g1)
    c: Coincident(g1,g2)
    c: Coincident(g2,g3)
    c: Coincident(g8,g0)
    c: Vertical(g0)
    c: Vertical(g2)
    c: Horizontal(g1)
    c: Symmetric(g2,g0,g4)
    c: PointOnObject(g4,g-2)
    c: DistanceY(g-1,g4) = 28
    c: DistanceX(g8,g3) = 50
    c: Angle(g5) = 3.14159
    c: Coincident(g5,g4)
    c: Vertical(g6)
    c: Coincident(g6,g5)
    c: Radius(g5) = 12
    c: Coincident(g5,g7)
    c: Coincident(g7,g3)
    c: Vertical(g7)
    c: Equal(g0,g2)
    c: Horizontal(g3)
    c: Horizontal(g8)
    c: Coincident(g6,g8)
    c: Distance(g4,g3) = 29
FEATURE [PartDesign::Pad] Pad005
  BaseFeature = -> Pad004
  Direction = (0,0,-1)
  Length = 44
  Length2 = 10
  Profile = -> Sketch006
  ReferenceAxis = -> Sketch006 [N_Axis]
  Refine = true
  Suppressed = false
  Type = 0
FEATURE [Sketcher::SketchObject] Sketch007
  ArcFitTolerance = 1e-06
  AttachmentSupport = -> [Pad005]
  FullyConstrained = false
  MakeInternals = false
  MapMode = 5
  Placement = pos=(0,-57,0) rot=(1,0,0;1.5708rad)
  sketch-geometry (5):
    g0: LineSegment StartX=21.5 StartY=-62.7172 StartZ=0 EndX=21.5 EndY=-27.7172 EndZ=0
    g1: LineSegment StartX=21.5 StartY=-27.7172 StartZ=0 EndX=-21.5 EndY=-27.7172 EndZ=0
    g2: LineSegment StartX=-21.5 StartY=-27.7172 StartZ=0 EndX=-21.5 EndY=-62.7172 EndZ=0
    g3: LineSegment StartX=-21.5 StartY=-62.7172 StartZ=0 EndX=21.5 EndY=-62.7172 EndZ=0
    g4: GeomPoint [constr] X=0 Y=-45.2172 Z=0
  constraints (12):
    c: Coincident(g0,g1)
    c: Coincident(g1,g2)
    c: Coincident(g2,g3)
    c: Coincident(g3,g0)
    c: Vertical(g0)
    c: Vertical(g2)
    c: Horizontal(g1)
    c: Horizontal(g3)
    c: Symmetric(g2,g0,g4)
    c: PointOnObject(g4,g-2)
    c: DistanceY(g2,g2) = 35
    c: DistanceX(g1,g1) = 43
FEATURE [PartDesign::Pocket] Pocket001
  BaseFeature = -> Pad005
  Direction = (0,1,-2e-16)
  Length = 53
  Length2 = 5
  Profile = -> Sketch007
  ReferenceAxis = -> Sketch007 [N_Axis]
  Refine = true
  Suppressed = false
  Type = 0
FEATURE [Sketcher::SketchObject] Sketch008
  ArcFitTolerance = 1e-06
  AttachmentSupport = -> [Pocket001]
  ExternalGeometry = -> [Pocket001]
  FullyConstrained = false
  MakeInternals = false
  MapMode = 5
  Placement = pos=(0,-42,0) rot=(1,0,0;1.5708rad)
  sketch-geometry (6):
    g0: LineSegment StartX=-32 StartY=-23 StartZ=0 EndX=-25 EndY=-23 EndZ=0
    g1: LineSegment StartX=-25 StartY=-23 StartZ=0 EndX=-25 EndY=-42.5619 EndZ=0
    g2: LineSegment StartX=-25 StartY=-42.5619 StartZ=0 EndX=-32 EndY=-23 EndZ=0
    g3: LineSegment StartX=32 StartY=-23 StartZ=0 EndX=25 EndY=-23 EndZ=0
    g4: LineSegment StartX=25 StartY=-42.5619 StartZ=0 EndX=32 EndY=-23 EndZ=0
    g5: LineSegment StartX=25 StartY=-23 StartZ=0 EndX=25 EndY=-42.5619 EndZ=0
  constraints (13):
    c: Coincident(g-3,g0)
    c: Coincident(g0,g-4)
    c: Coincident(g0,g1)
    c: Vertical(g1)
    c: Coincident(g1,g2)
    c: Coincident(g2,g0)
    c: Coincident(g-6,g3)
    c: Coincident(g3,g-6)
    c: Coincident(g4,g3)
    c: Coincident(g3,g5)
    c: Coincident(g5,g4)
    c: Vertical(g5)
    c: Horizontal(g1,g4)
FEATURE [PartDesign::Pad] Pad006
  BaseFeature = -> Pocket001
  Direction = (0,-1,2e-16)
  Length = 25
  Length2 = 10
  Profile = -> Sketch008
  ReferenceAxis = -> Sketch008 [N_Axis]
  Refine = true
  Reversed = true
  Suppressed = false
  Type = 0
FEATURE [Sketcher::SketchObject] Sketch009
  ArcFitTolerance = 1e-06
  AttachmentSupport = -> [Pad006]
  FullyConstrained = true
  MakeInternals = false
  MapMode = 5
  Placement = pos=(0,0,-23) rot=(0,0,1;0rad)
  expr: Constraints[10] = <<SpreadSheet>>.StepperCenterToScewHole
  expr: Constraints[11] = <<SpreadSheet>>.StepperCenterToScewHole
  expr: Constraints[12] = <<SpreadSheet>>.StepperCenterToScewHole
  expr: Constraints[13] = <<SpreadSheet>>.StepperCenterToScewHole
  expr: Constraints[3] = <<SpreadSheet>>.StepperCenterToScewHole
  expr: Constraints[4] = <<SpreadSheet>>.StepperCenterToScewHole
  expr: Constraints[8] = <<SpreadSheet>>.StepperCenterToScewHole
  expr: Constraints[9] = <<SpreadSheet>>.StepperCenterToScewHole
  sketch-geometry (5):
    g0: GeomPoint [constr] X=0 Y=-28 Z=0
    g1: Circle CenterX=-15.5 CenterY=-12.5 CenterZ=0 NormalX=0 NormalY=0 NormalZ=1 AngleXU=0 Radius=1.5
    g2: Circle CenterX=-15.5 CenterY=-43.5 CenterZ=0 NormalX=0 NormalY=0 NormalZ=1 AngleXU=0 Radius=1.5
    g3: Circle CenterX=15.5 CenterY=-43.5 CenterZ=0 NormalX=0 NormalY=0 NormalZ=1 AngleXU=0 Radius=1.5
    g4: Circle CenterX=15.5 CenterY=-12.5 CenterZ=0 NormalX=0 NormalY=0 NormalZ=1 AngleXU=0 Radius=1.5
  constraints (14):
    c: PointOnObject(g0,g-2)
    c: DistanceY(g0,g-1) = 28
    c: Diameter(g1) = 3
    c: Distance(g1,g-2) = 15.5
    c: DistanceY(g0,g1) = 15.5
    c: Diameter(g2) = 3
    c: Diameter(g3) = 3
    c: Diameter(g4) = 3
    c: Distance(g4,g-2) = 15.5
    c: DistanceY(g0,g4) = 15.5
    c: DistanceY(g3,g0) = 15.5
    c: DistanceY(g2,g0) = 15.5
    c: DistanceX(g2,g0) = 15.5
    c: DistanceX(g0,g3) = 15.5
FEATURE [PartDesign::Pocket] Pocket002
  BaseFeature = -> Pad006
  Direction = (0,0,-1)
  Length = 10
  Length2 = 5
  Profile = -> Sketch009
  ReferenceAxis = -> Sketch009 [N_Axis]
  Refine = true
  Suppressed = false
  Type = 1
FEATURE [Sketcher::SketchObject] Sketch012
  ArcFitTolerance = 1e-06
  AttachmentSupport = -> [Pocket002]
  FullyConstrained = true
  MakeInternals = false
  MapMode = 5
  expr: Constraints[0] = 6
  expr: Constraints[1] = 25
  expr: Constraints[2] = 25 mm
  sketch-geometry (1):
    g0: Circle CenterX=-25 CenterY=25 CenterZ=0 NormalX=0 NormalY=0 NormalZ=1 AngleXU=0 Radius=3
  constraints (3):
    c: Diameter(g0) = 6
    c: Distance(g0,g-2) = 25
    c: Distance(g0,g-1) = 25
FEATURE [PartDesign::Pocket] Pocket004
  BaseFeature = -> Pocket002
  Direction = (0,0,-1)
  Length = 10
  Length2 = 5
  Profile = -> Sketch012
  ReferenceAxis = -> Sketch012 [N_Axis]
  Refine = true
  Suppressed = false
  Type = 0
FEATURE [PartDesign::PolarPattern] PolarPattern
  Angle = 360
  Axis = -> Sketch012 [N_Axis]
  BaseFeature = -> Pocket004
  Mode = 0
  Occurrences = 4
  Offset = 120
  Originals = -> [Pocket004]
  Refine = true
  Suppressed = false
  TransformMode = 0
FEATURE [PartDesign::Chamfer] Chamfer
  Angle = 45
  Base = -> PolarPattern [Edge11,Edge2,Edge69,Edge54,Edge35,Edge57]
  BaseFeature = -> PolarPattern
  ChamferType = 0
  FlipDirection = false
  Refine = true
  Size = 5
  Size2 = 1
  SupportTransform = false
  Suppressed = false
  UseAllEdges = false
FEATURE [Sketcher::SketchObject] Sketch013
  ArcFitTolerance = 1e-06
  AttachmentSupport = -> [Chamfer]
  ExternalGeometry = -> [Chamfer]
  FullyConstrained = false
  MakeInternals = false
  MapMode = 5
  Placement = pos=(0,1,0) rot=(0,0.707107,0.707107;3.14159rad)
  sketch-geometry (4):
    g0: LineSegment StartX=-12 StartY=-62.7172 StartZ=0 EndX=12 EndY=-62.7172 EndZ=0
    g1: LineSegment StartX=12 StartY=-62.7172 StartZ=0 EndX=12 EndY=-49.3568 EndZ=0
    g2: LineSegment StartX=-12 StartY=-49.3568 StartZ=0 EndX=-12 EndY=-62.7172 EndZ=0
    g3: ArcOfCircle CenterX=0 CenterY=-49.3568 CenterZ=0 NormalX=0 NormalY=0 NormalZ=1 AngleXU=0 Radius=12 StartAngle=0 EndAngle=3.14159
  constraints (10):
    c: Coincident(g0,g1)
    c: Coincident(g2,g0)
    c: Horizontal(g0)
    c: Vertical(g1)
    c: Vertical(g2)
    c: Distance(g1,g2) = 24
    c: Coincident(g0,g-3)
    c: Symmetric(g1,g2,g3)
    c: Coincident(g3,g2)
    c: Coincident(g3,g1)
FEATURE [PartDesign::Pocket] Pocket
  BaseFeature = -> Chamfer
  Direction = (0,-1,2e-16)
  Length = 5
  Length2 = 5
  Profile = -> Sketch013
  ReferenceAxis = -> Sketch013 [N_Axis]
  Refine = true
  Suppressed = false
  Type = 0
FEATURE [Sketcher::SketchObject] Sketch
  ArcFitTolerance = 1e-06
  AttachmentSupport = -> [Pocket]
  FullyConstrained = true
  MakeInternals = false
  MapMode = 5
  Placement = pos=(0,0,-23) rot=(1,0,0;3.14159rad)
  sketch-geometry (16):
    g0: LineSegment StartX=-32 StartY=17 StartZ=0 EndX=-25 EndY=17 EndZ=0
    g1: LineSegment StartX=-25 StartY=17 StartZ=0 EndX=-25 EndY=7 EndZ=0
    g2: LineSegment StartX=-25 StartY=7 StartZ=0 EndX=-20 EndY=2 EndZ=0
    g3: LineSegment StartX=-20 StartY=2 StartZ=0 EndX=-20 EndY=-15 EndZ=0
    g4: LineSegment StartX=-20 StartY=-15 StartZ=0 EndX=-15 EndY=-20 EndZ=0
    g5: LineSegment StartX=-15 StartY=-20 StartZ=0 EndX=15 EndY=-20 EndZ=0
    g6: LineSegment StartX=15 StartY=-20 StartZ=0 EndX=20 EndY=-15 EndZ=0
    g7: LineSegment StartX=20 StartY=-15 StartZ=0 EndX=20 EndY=2 EndZ=0
    g8: LineSegment StartX=20 StartY=2 StartZ=0 EndX=25 EndY=7 EndZ=0
    g9: LineSegment StartX=25 StartY=7 StartZ=0 EndX=25 EndY=17 EndZ=0
    g10: LineSegment StartX=25 StartY=17 StartZ=0 EndX=32 EndY=17 EndZ=0
    g11: LineSegment StartX=32 StartY=17 StartZ=0 EndX=32 EndY=-27 EndZ=0
    g12: LineSegment StartX=32 StartY=-27 StartZ=0 EndX=27 EndY=-32 EndZ=0
    g13: LineSegment StartX=27 StartY=-32 StartZ=0 EndX=-27 EndY=-32 EndZ=0
    g14: LineSegment StartX=-27 StartY=-32 StartZ=0 EndX=-32 EndY=-27 EndZ=0
    g15: LineSegment StartX=-32 StartY=-27 StartZ=0 EndX=-32 EndY=17 EndZ=0
  constraints (48):
    c: Horizontal(g0)
    c: Coincident(g0,g1)
    c: Vertical(g1)
    c: Coincident(g1,g2)
    c: Coincident(g2,g3)
    c: Vertical(g3)
    c: Coincident(g3,g4)
    c: Coincident(g4,g5)
    c: Horizontal(g5)
    c: Coincident(g5,g6)
    c: Coincident(g6,g7)
    c: Vertical(g7)
    c: Coincident(g7,g8)
    c: Coincident(g8,g9)
    c: Vertical(g9)
    c: Coincident(g9,g10)
    c: Horizontal(g10)
    c: Coincident(g10,g11)
    c: Vertical(g11)
    c: Coincident(g11,g12)
    c: Coincident(g12,g13)
    c: Horizontal(g13)
    c: Coincident(g13,g14)
    c: Coincident(g14,g15)
    c: Coincident(g15,g0)
    c: Vertical(g15)
    c: Distance(g-2,g15) = 32
    c: Distance(g-1,g0) = 17
    c: Distance(g0,g0) = 7
    c: DistanceY(g1,g1) = 10
    c: Distance(g15,g3) = 12
    c: Angle(g2,g1) = 2.35619
    c: Angle(g14,g15) = 2.35619
    c: Distance(g-1,g13) = 32
    c: DistanceX(g10,g10) = 7
    c: Distance(g-2,g11) = 32
    c: DistanceY(g9,g9) = 10
    c: Angle(g9,g8) = 2.35619
    c: Distance(g-1,g10) = 17
    c: Distance(g7,g11) = 12
    c: DistanceY(g14,g-1) = 27
    c: DistanceY(g11,g-1) = 27
    c: Angle(g11,g12) = 2.35619
    c: Angle(g4,g3) = 2.35619
    c: Angle(g7,g6) = 2.35619
    c: Distance(g-1,g5) = 20
    c: DistanceX(g4,g-1) = 15
    c: Distance(g5,g-2) = 15
FEATURE [PartDesign::Pad] Pad
  BaseFeature = -> Pocket
  Direction = (0,0,-1)
  Length = 44
  Length2 = 10
  Profile = -> Sketch
  ReferenceAxis = -> Sketch [N_Axis]
  Refine = true
  Suppressed = false
  Type = 0
FEATURE [Sketcher::SketchObject] Sketch014
  ArcFitTolerance = 1e-06
  AttachmentSupport = -> [Pad]
  ExternalGeometry = -> [Pad]
  FullyConstrained = true
  MakeInternals = false
  MapMode = 5
  Placement = pos=(-25,0,0) rot=(0.57735,-0.57735,-0.57735;2.0944rad)
  sketch-geometry (2):
    g0: Circle CenterX=49.5 CenterY=-33 CenterZ=0 NormalX=0 NormalY=0 NormalZ=1 AngleXU=0 Radius=1.5
    g1: Circle CenterX=49.5 CenterY=-56 CenterZ=0 NormalX=0 NormalY=0 NormalZ=1 AngleXU=0 Radius=1.5
  constraints (6):
    c: Diameter(g0) = 3
    c: Diameter(g1) = 3
    c: Distance(g0,g-3) = 7.5
    c: DistanceY(g0,g-3) = 10
    c: Distance(g1,g-3) = 7.5
    c: DistanceY(g1,g0) = 23
FEATURE [PartDesign::Pocket] Pocket005
  BaseFeature = -> Pad
  Direction = (1,0,0)
  Length = 5
  Length2 = 5
  Profile = -> Sketch014
  ReferenceAxis = -> Sketch014 [N_Axis]
  Refine = true
  Suppressed = false
  Type = 1
FEATURE [Sketcher::SketchObject] Sketch015
  ArcFitTolerance = 1e-06
  AttachmentSupport = -> [Pocket005]
  ExternalGeometry = -> [Pocket005]
  FullyConstrained = true
  MakeInternals = false
  MapMode = 5
  Placement = pos=(-25,0,0) rot=(0.57735,-0.57735,-0.57735;2.0944rad)
  sketch-geometry (3):
    g0: LineSegment StartX=22 StartY=-67 StartZ=0 EndX=42 EndY=-67 EndZ=0
    g1: LineSegment StartX=42 StartY=-67 StartZ=0 EndX=42 EndY=-47 EndZ=0
    g2: LineSegment StartX=42 StartY=-47 StartZ=0 EndX=22 EndY=-67 EndZ=0
  constraints (9):
    c: PointOnObject(g0,g-3)
    c: PointOnObject(g0,g-3)
    c: Coincident(g0,g1)
    c: Vertical(g1)
    c: Coincident(g1,g2)
    c: Coincident(g2,g0)
    c: Angle(g0,g2) = 0.785398
    c: Distance(g-3,g1) = 15
    c: DistanceX(g0,g0) = 20
FEATURE [PartDesign::Pad] Pad007
  BaseFeature = -> Pocket005
  Direction = (-1,0,0)
  Length = 15
  Length2 = 10
  Profile = -> Sketch015
  ReferenceAxis = -> Sketch015 [N_Axis]
  Refine = true
  Suppressed = false
  Type = 0
FEATURE [Sketcher::SketchObject] Sketch016
  ArcFitTolerance = 1e-06
  AttachmentSupport = -> [Pad007]
  ExternalGeometry = -> [Pad007]
  FullyConstrained = true
  MakeInternals = false
  MapMode = 5
  Placement = pos=(0,-42,0) rot=(1,0,0;1.5708rad)
  sketch-geometry (1):
    g0: Circle CenterX=-32.5 CenterY=-57 CenterZ=0 NormalX=0 NormalY=0 NormalZ=1 AngleXU=0 Radius=1.5
  constraints (3):
    c: Diameter(g0) = 3
    c: Distance(g0,g-3) = 7.5
    c: DistanceY(g-3,g0) = 10
FEATURE [PartDesign::Pocket] Pocket006
  BaseFeature = -> Pad007
  Direction = (0,1,-2e-16)
  Length = 20
  Length2 = 5
  Profile = -> Sketch016
  ReferenceAxis = -> Sketch016 [N_Axis]
  Refine = true
  Suppressed = false
  Type = 0
FEATURE [Sketcher::SketchObject] Sketch017
  ArcFitTolerance = 1e-06
  AttachmentSupport = -> [Pocket006]
  ExternalGeometry = -> [Pocket006]
  FullyConstrained = true
  MakeInternals = false
  MapMode = 5
  Placement = pos=(0,0,-67) rot=(1,0,0;3.14159rad)
  sketch-geometry (1):
    g0: Circle CenterX=-32.5 CenterY=32 CenterZ=0 NormalX=0 NormalY=0 NormalZ=1 AngleXU=0 Radius=1.5
  constraints (3):
    c: Diameter(g0) = 3
    c: Distance(g0,g-3) = 10
    c: DistanceX(g0,g-3) = 7.5
FEATURE [PartDesign::Pocket] Pocket007
  BaseFeature = -> Pocket006
  Direction = (0,0,1)
  Length = 20
  Length2 = 5
  Profile = -> Sketch017
  ReferenceAxis = -> Sketch017 [N_Axis]
  Refine = true
  Suppressed = false
  Type = 0
FEATURE [Sketcher::SketchObject] Sketch018
  ArcFitTolerance = 1e-06
  AttachmentOffset = pos=(0,0,-5) rot=(0,0,1;0rad)
  AttachmentSupport = -> [Pocket007]
  ExternalGeometry = -> [Pocket007]
  FullyConstrained = true
  MakeInternals = false
  MapMode = 5
  Placement = pos=(0,0,-62) rot=(1,0,0;3.14159rad)
  sketch-geometry (5):
    g0: LineSegment StartX=-28 StartY=27 StartZ=0 EndX=-28 EndY=37 EndZ=0
    g1: LineSegment StartX=-28 StartY=37 StartZ=0 EndX=-37 EndY=37 EndZ=0
    g2: LineSegment StartX=-37 StartY=37 StartZ=0 EndX=-37 EndY=27 EndZ=0
    g3: LineSegment StartX=-37 StartY=27 StartZ=0 EndX=-28 EndY=27 EndZ=0
    g4: GeomPoint [constr] X=-32.5 Y=32 Z=0
  constraints (13):
    c: Coincident(g0,g1)
    c: Coincident(g1,g2)
    c: Coincident(g2,g3)
    c: Coincident(g3,g0)
    c: Vertical(g0)
    c: Vertical(g2)
    c: Horizontal(g1)
    c: Horizontal(g3)
    c: Symmetric(g2,g0,g4)
    c: Distance(g4,g-3) = 10
    c: Distance(g4,g-4) = 7.5
    c: Distance(g-3,g1) = 5
    c: Distance(g-4,g2) = 3
FEATURE [PartDesign::Pocket] Pocket008
  BaseFeature = -> Pocket007
  Direction = (0,0,1)
  Length = 15
  Length2 = 5
  Profile = -> Sketch018
  ReferenceAxis = -> Sketch018 [N_Axis]
  Refine = true
  Suppressed = false
  Type = 0
FEATURE [PartDesign::Mirrored] Mirrored
  BaseFeature = -> Pocket008
  MirrorPlane = -> YZ_Plane001
  Originals = -> [Pad007,Pocket006,Pocket007,Pocket008]
  Refine = true
  Suppressed = false
  TransformMode = 0
FEATURE [Sketcher::SketchObject] Sketch019
  ArcFitTolerance = 1e-06
  AttachmentSupport = -> [Mirrored]
  ExternalGeometry = -> [Mirrored]
  FullyConstrained = false
  MakeInternals = false
  MapMode = 5
  Placement = pos=(0,32,0) rot=(0,0.707107,0.707107;3.14159rad)
  sketch-geometry (4):
    g0: LineSegment StartX=-8 StartY=-63 StartZ=0 EndX=8 EndY=-63 EndZ=0
    g1: LineSegment StartX=8 StartY=-63 StartZ=0 EndX=8 EndY=-50.4111 EndZ=0
    g2: LineSegment StartX=-8 StartY=-50.4111 StartZ=0 EndX=-8 EndY=-63 EndZ=0
    g3: ArcOfCircle CenterX=0 CenterY=-50.4853 CenterZ=0 NormalX=0 NormalY=0 NormalZ=1 AngleXU=0 Radius=8.00034 StartAngle=0.009278 EndAngle=3.13231
  constraints (11):
    c: Horizontal(g0)
    c: Coincident(g0,g1)
    c: Vertical(g1)
    c: Coincident(g2,g0)
    c: Vertical(g2)
    c: Distance(g-3,g0) = 4
    c: Distance(g-2,g2) = 8
    c: Distance(g-2,g1) = 8
    c: PointOnObject(g3,g-2)
    c: Coincident(g3,g2)
    c: Coincident(g3,g1)
FEATURE [PartDesign::Pocket] Pocket009
  BaseFeature = -> Mirrored
  Direction = (0,-1,2e-16)
  Length = 15
  Length2 = 5
  Profile = -> Sketch019
  ReferenceAxis = -> Sketch019 [N_Axis]
  Refine = true
  Suppressed = false
  Type = 0
FEATURE [Sketcher::SketchObject] Sketch020
  ArcFitTolerance = 1e-06
  AttachmentSupport = -> [Pocket009]
  FullyConstrained = true
  MakeInternals = false
  MapMode = 5
  Placement = pos=(0,-1.39e-14,-63) rot=(0,0,1;0rad)
  sketch-geometry (1):
    g0: Circle CenterX=0 CenterY=27.5 CenterZ=0 NormalX=0 NormalY=0 NormalZ=1 AngleXU=0 Radius=1.5
  constraints (3):
    c: PointOnObject(g0,g-2)
    c: Diameter(g0) = 3
    c: DistanceY(g-1,g0) = 27.5
FEATURE [PartDesign::Pocket] Pocket010
  BaseFeature = -> Pocket009
  Direction = (0,0,-1)
  Length = 5
  Length2 = 5
  Profile = -> Sketch020
  ReferenceAxis = -> Sketch020 [N_Axis]
  Refine = true
  Suppressed = false
  Type = 0
FEATURE [PartDesign::Body] Body001  label="BodyHolder"
  AllowCompound = false
  Group = -> [Sketch005,Pad004,Sketch006,Pad005,Sketch007,Pocket001,Sketch008,Pad006,Sketch009,Pocket002,Sketch012,Pocket004,PolarPattern,Chamfer,Sketch013,Pocket,Sketch,Pad,Sketch014,Pocket005,Sketch015,Pad007,Sketch016,Pocket006,Sketch017,Pocket007,Sketch018,Pocket008,Mirrored,Sketch019,Pocket009,Sketch020,Pocket010]
  Origin = -> Origin001
  Tip = -> Pocket010
COMPONENT P3 — same part as P1; its construction recipe is shown at P1.
COMPONENT P4 — same part as P1; its construction recipe is shown at P1.
COMPONENT P5 — recipe-attached ("Stick251", modeled in this document).
Construction recipe (the document's own serialized feature program — sketch geometry with constraints, then the solid features built on it; lengths are millimeters unless a unit is written):

FEATURE [Sketcher::SketchObject] Sketch038
  ArcFitTolerance = 1e-06
  AttachmentSupport = -> [XY_Plane003]
  FullyConstrained = false
  MakeInternals = false
  MapMode = 5
  sketch-geometry (21):
    g0: LineSegment StartX=-7.5 StartY=-7.5 StartZ=0 EndX=-3 EndY=-7.5 EndZ=0
    g1: LineSegment StartX=7.5 StartY=-7.5 StartZ=0 EndX=7.5 EndY=-3 EndZ=0
    g2: LineSegment StartX=7.5 StartY=7.5 StartZ=0 EndX=3 EndY=7.5 EndZ=0
    g3: LineSegment StartX=-7.5 StartY=7.5 StartZ=0 EndX=-7.5 EndY=3 EndZ=0
    g4: GeomPoint [constr] X=0 Y=0 Z=0
    g5: LineSegment StartX=3 StartY=-7.5 StartZ=0 EndX=3 EndY=-4 EndZ=0
    g6: LineSegment StartX=3 StartY=-4 StartZ=0 EndX=-3 EndY=-4 EndZ=0
    g7: LineSegment StartX=-3 StartY=-4 StartZ=0 EndX=-3 EndY=-7.5 EndZ=0
    g8: LineSegment StartX=7.5 StartY=-3 StartZ=0 EndX=4 EndY=-3 EndZ=0
    g9: LineSegment StartX=4 StartY=-3 StartZ=0 EndX=4 EndY=3 EndZ=0
    g10: LineSegment StartX=4 StartY=3 StartZ=0 EndX=7.5 EndY=3 EndZ=0
    g11: LineSegment StartX=3 StartY=7.5 StartZ=0 EndX=3 EndY=4 EndZ=0
    g12: LineSegment StartX=3 StartY=4 StartZ=0 EndX=-3 EndY=4 EndZ=0
    g13: LineSegment StartX=-3 StartY=4 StartZ=0 EndX=-3 EndY=7.5 EndZ=0
    g14: LineSegment StartX=-7.5 StartY=3 StartZ=0 EndX=-4 EndY=3 EndZ=0
    g15: LineSegment StartX=-4 StartY=3 StartZ=0 EndX=-4 EndY=-3 EndZ=0
    g16: LineSegment StartX=-4 StartY=-3 StartZ=0 EndX=-7.5 EndY=-3 EndZ=0
    g17: LineSegment StartX=3 StartY=-7.5 StartZ=0 EndX=7.5 EndY=-7.5 EndZ=0
    g18: LineSegment StartX=7.5 StartY=3 StartZ=0 EndX=7.5 EndY=7.5 EndZ=0
    g19: LineSegment StartX=-3 StartY=7.5 StartZ=0 EndX=-7.5 EndY=7.5 EndZ=0
    g20: LineSegment StartX=-7.5 StartY=-3 StartZ=0 EndX=-7.5 EndY=-7.5 EndZ=0
  constraints (56):
    c: Coincident(g17,g1)
    c: Coincident(g18,g2)
    c: Coincident(g19,g3)
    c: Coincident(g20,g0)
    c: Horizontal(g0)
    c: Horizontal(g2)
    c: Vertical(g1)
    c: Vertical(g3)
    c: Symmetric(g2,g0,g4)
    c: Distance(g1,g20) = 15
    c: Distance(g0,g19) = 15
    c: Coincident(g4,g-1)
    c: PointOnObject(g5,g17)
    c: Vertical(g5)
    c: Coincident(g5,g6)
    c: Horizontal(g6)
    c: Coincident(g6,g7)
    c: Vertical(g7)
    c: Horizontal(g8)
    c: Coincident(g8,g9)
    c: Vertical(g9)
    c: Coincident(g9,g10)
    c: PointOnObject(g10,g18)
    c: Horizontal(g10)
    c: Vertical(g11)
    c: Coincident(g11,g12)
    c: Horizontal(g12)
    c: Coincident(g12,g13)
    c: PointOnObject(g13,g19)
    c: Vertical(g13)
    c: Horizontal(g14)
    c: Coincident(g14,g15)
    c: Vertical(g15)
    c: Coincident(g15,g16)
    c: PointOnObject(g16,g20)
    c: Horizontal(g16)
    c: Coincident(g0,g7)
    c: PointOnObject(g17,g5)
    c: Coincident(g1,g8)
    c: PointOnObject(g18,g10)
    c: Coincident(g2,g11)
    c: PointOnObject(g19,g13)
    c: Coincident(g3,g14)
    c: PointOnObject(g20,g16)
    c: Distance(g-1,g6) = 4
    c: Distance(g-2,g15) = 4
    c: Distance(g-1,g12) = 4
    c: Distance(g-2,g9) = 4
    c: Distance(g-2,g5) = 3
    c: Distance(g-1,g8) = 3
    c: Distance(g-1,g10) = 3
    c: Distance(g-2,g7) = 3
    c: Distance(g-1,g16) = 3
    c: Distance(g-1,g14) = 3
    c: Distance(g-2,g13) = 3
    c: Distance(g-2,g11) = 3
FEATURE [PartDesign::Pad] Pad014
  Direction = (0,0,1)
  Length = 250
  Length2 = 10
  Profile = -> Sketch038
  ReferenceAxis = -> Sketch038 [N_Axis]
  Refine = true
  Suppressed = false
  Type = 0
FEATURE [PartDesign::Body] Body003  label="Stick250"
  AllowCompound = false
  Group = -> [Sketch038,Pad014]
  Origin = -> Origin003
  Placement = pos=(24.5,117.2,-74.5) rot=(0,-0.707107,0.707107;3.14159rad)
  Tip = -> Pad014
COMPONENT P6 — same part as P1; its construction recipe is shown at P1.
COMPONENT P7 — same part as P1; its construction recipe is shown at P1.
COMPONENT P8 — same part as P1; its construction recipe is shown at P1.
COMPONENT P9 — same part as P1; its construction recipe is shown at P1.
COMPONENT P10 — same part as P5; its construction recipe is shown at P5.
COMPONENT P11 — same part as P5; its construction recipe is shown at P5.
COMPONENT P12 — geometry summary ("RobotShell"; no construction recipe available for this part):
  bounding box: 563.9 x 210.0 x 192.5 mm
  tessellated surface: 46,850 triangles
  volume: 2213842 mm^3 (10% of its bounding box)
COMPONENT P13 — geometry summary ("NUC_BE_Chassis_Tall_18WW10"; no construction recipe available for this part):
  bounding box: 117.0 x 112.5 x 51.2 mm
  tessellated surface: 318,640 triangles
  volume: 186192 mm^3 (28% of its bounding box)
PROVENANCE & LICENSES
A FreeCAD (.FCStd) document from a public repository crawl; recipes are the document's own serialized feature recipes (and, for linked parts, companion documents' recipes).
License: as declared in the source repository (recorded in the dataset sidecar).
